# Revit family: Furniture-Console_Table-KALLISTA-Script-P78575
name_source: partatom
category: Specialty Equipment
units: mm (PartAtom-declared; Revit-internal decimal feet)

## family parameters
Cut with Voids When Loaded = No
Host = Face
Maintain Annotation Orientation = No
OmniClass Number = 23.21.19.15
OmniClass Title = Specialty Casework
Part Type = Normal
Room Calculation Point = No
Round Connector Dimension = Use Diameter
Shared = No

## types (1)
- BL-Matte Black
    ADA Compliant = No
    Assembly Code = E20
    Date Modified = 06/03/2025
    Default Elevation = 48"
    Description = Wall-hung Console
    Finish = Kallista-Metal-BL-Matte_Black
    Height = 21"
    Length = 19 9/16"
    Manufacturer = Kallista  Co.
    Master Format 2014 = 06 41 93
    Master Format 2014 Name = Cabinet and Drawer Hardware
    Material = Premium Metal Construction
    Model = P78575-00-BL
    Product Documentation Link = https://techcomm.kohler.com
    Product Name = Script
    Product Page URL = https://www.kallista.com
    Type = 1
    URL = https://www.kallista.com
    WaterSense Certified = No
    Width = 27"

## geometry (parser evidence)
native form markers: Sweep x5
no freeform markers — native parametric forms only
